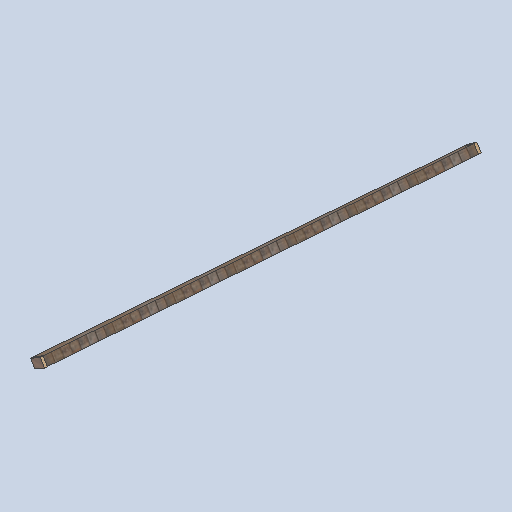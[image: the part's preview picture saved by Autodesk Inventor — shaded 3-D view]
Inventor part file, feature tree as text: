
AUTODESK INVENTOR PART (.ipt)
format: ipt  version: 2024.2 (Build 282272000, 272)  size: 129,536 bytes
history: native  units: in
note: dims shown in document units (in); Inventor stores cm internally (conversion verified against a paired STEP export)
features: sketch x4, other x3, plane x2
ambient origin geometry x8: Origin, YZ Plane, XZ Plane, XY Plane, X Axis, Y Axis, Z Axis, Center Point
bodies: Solid1 (feature_tree)
feature tree (9):
  other  "support_beam_segment_0103_MIR.ipt"
  other  "Solid1::support_beam_segment_0103_MIR.ipt"
  other  "TaggingFeature1"
  sketch  "Sketch1"  dims[d0=0.3937in]
  sketch  "Sketch2"
  sketch  "Sketch3"
  sketch  "Sketch4"
  plane  "Work Plane1"
  plane  "Work Plane2"
